# Revit family: Kee_Safety_KEEWALK_DEFAULT
name_source: partatom
category: Generic Models
units: mm (PartAtom-declared; Revit-internal decimal feet)

## family parameters
Can host rebar = No
Cut with Voids When Loaded = No
Host = Face
Maintain Annotation Orientation = No
Part Type = Normal
Room Calculation Point = No
Round Connector Dimension = Use Diameter
Shared = No

## types (2) — shared parameters
Base Material = Base Material
Default Elevation = 1219 mm
Railing Material = Kee Rail
Step Angle = 25.00°
Step Brck position = 267 mm  [stored 0.875984 ft]
Step Material = Kee Steel
full steps pitch = 2450 mm  [stored 8.03806 ft]
part = No
step length = 534 mm  [stored 1.75197 ft]

## per-type parameters (varying)
| type | Overall Length |
| KWM17 3M STEPS MODULE 25 TO 35 DEG | 3000 mm  [stored 9.84252 ft] |
| KWM18 1,1M STEPS MODULE 25 TO 35 DEG | 1330 mm  [stored 4.36352 ft] |

note: [stored X ft] marks values corroborated as IEEE doubles in the binary element streams (Revit-internal decimal feet)

## geometry (parser evidence)
native form markers: Sweep x3
no freeform markers — native parametric forms only
